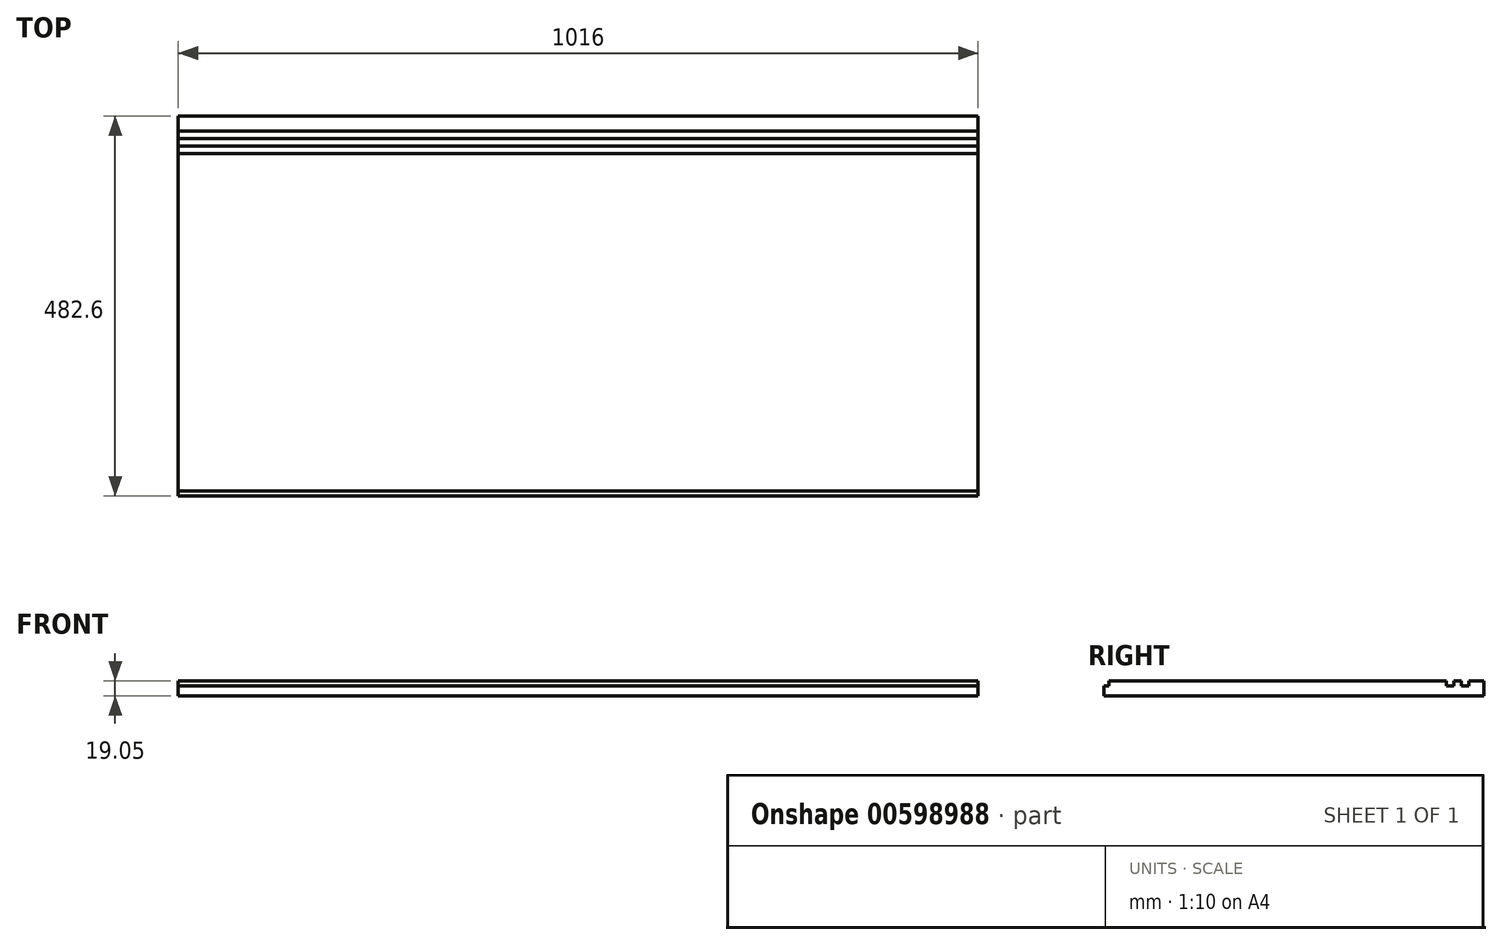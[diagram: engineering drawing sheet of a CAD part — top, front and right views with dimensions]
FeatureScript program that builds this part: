
annotation { "Feature Type Name" : "Feature", "Feature Type Description" : "" }
export const myFeature = defineFeature(function(context is Context, id is Id, definition is map)
    precondition{}
    {
        {
            var Q0;
            Q0=qCreatedBy(makeId("Top.planeOp"),FACE);
            var sketch = newSketch(context, id + "F0", { "sketchPlane" : qUnion([Q0])});
            skLineSegment(sketch, "E0.bottom", {"start": v(15.88, 14.06) * mm, "end": v(1031.88, 14.06) * mm});
            skLineSegment(sketch, "E0.top", {"start": v(15.88, 496.66) * mm, "end": v(1031.88, 496.66) * mm});
            skLineSegment(sketch, "E0.left", {"start": v(15.88, 14.06) * mm, "end": v(15.88, 496.66) * mm});
            skLineSegment(sketch, "E0.right", {"start": v(1031.88, 14.06) * mm, "end": v(1031.88, 496.66) * mm});
            skSolve(sketch);
        }
        {
            var Q0;
            Q0 = qSketchRegion(id + "F0", true);
            extrude(context, id + "F1", {"entities" : qUnion([Q0]), "depth" : 19.05 * mm, "offsetDistance" : 25.4 * mm});
        }
        {
            var Q0;
            Q0=makeQuery(id+"F1.opExtrude","CAP_FACE",FACE,{"disambiguationData":[OSD([sQuery(id+"F0.wireOp",EDGE,"E0.bottom"),sQuery(id+"F0.wireOp",EDGE,"E0.top"),sQuery(id+"F0.wireOp",EDGE,"E0.left"),sQuery(id+"F0.wireOp",EDGE,"E0.right")])],"isStart":false});
            var sketch = newSketch(context, id + "F2", { "sketchPlane" : qUnion([Q0])});
            skLineSegment(sketch, "E1.bottom", {"start": v(15.88, 477.6) * mm, "end": v(1031.88, 477.6) * mm});
            skLineSegment(sketch, "E1.top", {"start": v(15.88, 468.08) * mm, "end": v(1031.88, 468.08) * mm});
            skLineSegment(sketch, "E1.left", {"start": v(15.88, 477.6) * mm, "end": v(15.88, 468.08) * mm});
            skLineSegment(sketch, "E1.right", {"start": v(1031.88, 477.6) * mm, "end": v(1031.88, 468.08) * mm});
            skLineSegment(sketch, "E2.bottom", {"start": v(15.88, 458.56) * mm, "end": v(1031.88, 458.56) * mm});
            skLineSegment(sketch, "E2.top", {"start": v(15.88, 449.03) * mm, "end": v(1031.88, 449.03) * mm});
            skLineSegment(sketch, "E2.left", {"start": v(15.88, 458.56) * mm, "end": v(15.88, 449.03) * mm});
            skLineSegment(sketch, "E2.right", {"start": v(1031.88, 458.56) * mm, "end": v(1031.88, 449.03) * mm});
            skLineSegment(sketch, "E3", {"start": v(15.88, 468.08) * mm, "end": v(15.88, 458.56) * mm, "construction": true});
            skLineSegment(sketch, "E4.bottom", {"start": v(15.88, 14.06) * mm, "end": v(1031.88, 14.06) * mm});
            skLineSegment(sketch, "E4.top", {"start": v(15.88, 20.4) * mm, "end": v(1031.88, 20.4) * mm});
            skLineSegment(sketch, "E4.left", {"start": v(15.88, 14.06) * mm, "end": v(15.88, 20.4) * mm});
            skLineSegment(sketch, "E4.right", {"start": v(1031.88, 14.06) * mm, "end": v(1031.88, 20.4) * mm});
            skSolve(sketch);
        }
        {
            var Q0;
            Q0 = qSketchRegion(id + "F2", true);
            extrude(context, id + "F3", {"entities" : qUnion([Q0]), "operationType" : NewBodyOperationType.REMOVE, "oppositeDirection" : true, "depth" : 6.35 * mm, "offsetDistance" : 25.4 * mm});
        }
    });
